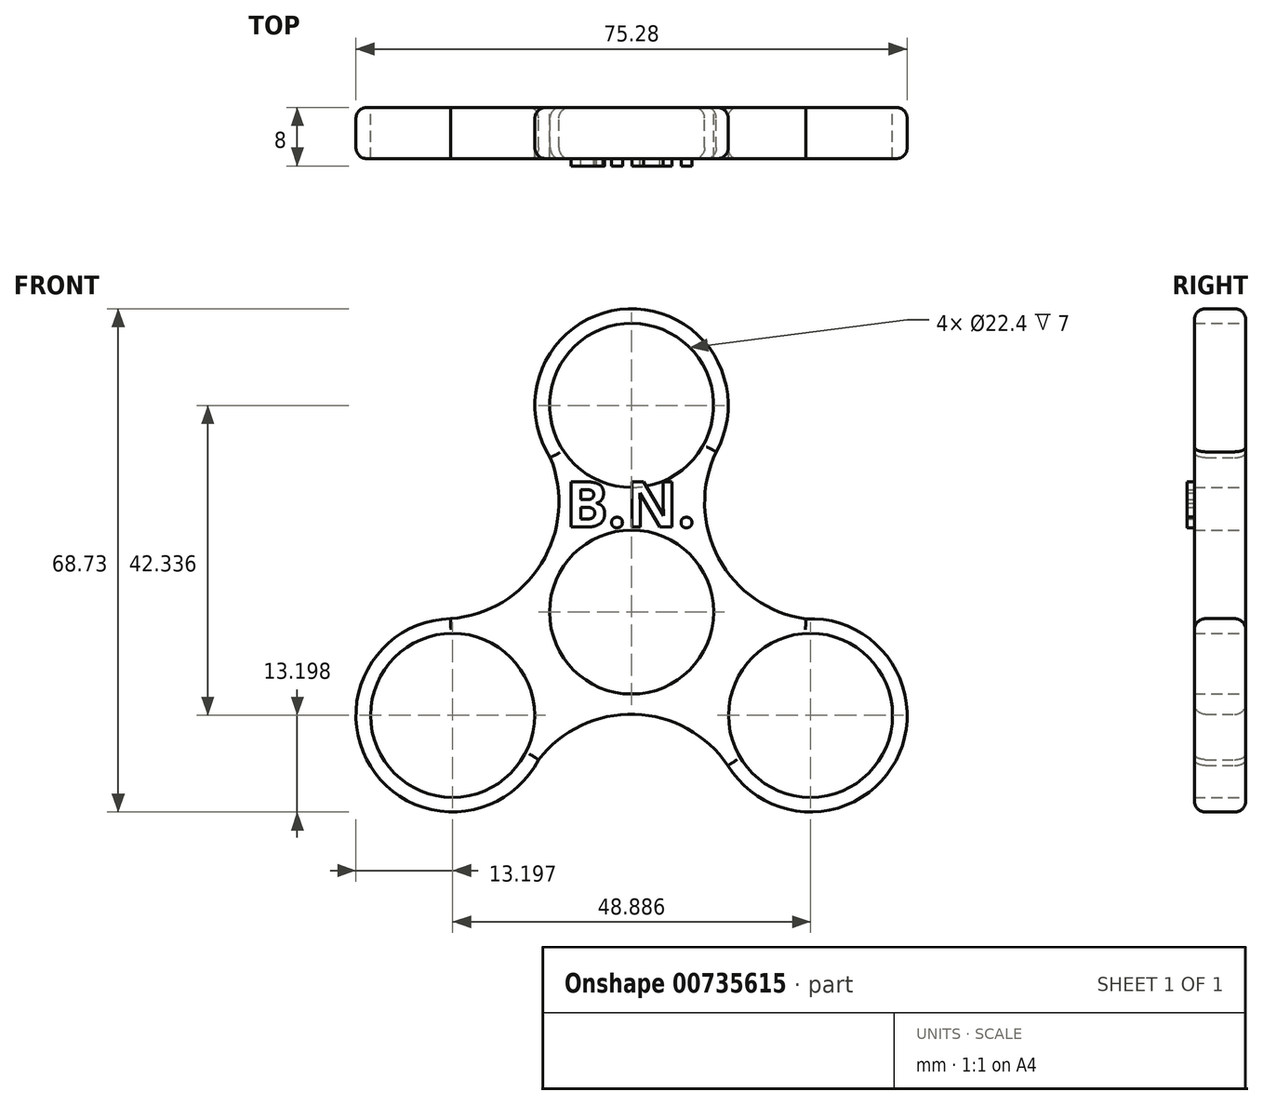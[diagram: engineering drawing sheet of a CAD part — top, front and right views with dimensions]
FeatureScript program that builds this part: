
annotation { "Feature Type Name" : "Feature", "Feature Type Description" : "" }
export const myFeature = defineFeature(function(context is Context, id is Id, definition is map)
    precondition{}
    {
        {
            var Q0;
            Q0=qCreatedBy(makeId("Front.planeOp"),FACE);
            var sketch = newSketch(context, id + "F0", { "sketchPlane" : qUnion([Q0])});
            skCircle(sketch, "E0", {"center": v(0, 0) * mm, "radius": 11.2 * mm});
            skCircle(sketch, "E1", {"center": v(0, 28.22) * mm, "radius": 11.2 * mm});
            skArc(sketch, "E2", {"start": v(11.57, 21.88) * mm, "mid": v(-0.46, 41.42) * mm, "end": v(-11.1, 21.09) * mm});
            skArc(sketch, "E3.1.0", {"start": v(-24.73, -0.92) * mm, "mid": v(-35.64, -21.1) * mm, "end": v(-12.71, -20.16) * mm});
            skCircle(sketch, "E3.1.1", {"center": v(-24.44, -14.11) * mm, "radius": 11.2 * mm});
            skArc(sketch, "E3.2.0", {"start": v(13.16, -20.96) * mm, "mid": v(36.1, -20.3) * mm, "end": v(23.81, -0.93) * mm});
            skCircle(sketch, "E3.2.1", {"center": v(24.44, -14.11) * mm, "radius": 11.2 * mm});
            skLineSegment(sketch, "E4", {"start": v(-12.1, 6.98) * mm, "end": v(-12.22, 7.06) * mm, "construction": true});
            skArc(sketch, "E5", {"start": v(-24.73, -0.92) * mm, "mid": v(-11.3, 8.55) * mm, "end": v(-13.29, 24.86) * mm});
            skArc(sketch, "E6.1.0", {"start": v(13.16, -20.96) * mm, "mid": v(-1.75, -14.06) * mm, "end": v(-14.89, -23.94) * mm});
            skArc(sketch, "E6.2.0", {"start": v(11.57, 21.88) * mm, "mid": v(13.05, 5.5) * mm, "end": v(28.17, -0.92) * mm});
            skLineSegment(sketch, "E7.trimOffspring", {"start": v(-13.27, 5.25) * mm, "end": v(-11.11, 8.98) * mm, "construction": true});
            skLineSegment(sketch, "E8.trimOffspring", {"start": v(-6.6, 16.8) * mm, "end": v(-5.6, 18.52) * mm, "construction": true});
            skSolve(sketch);
        }
        {
            var Q0;
            Q0 = qSketchRegion(id + "F0", true);
            extrude(context, id + "F1", {"entities" : qUnion([Q0]), "depth" : 7 * mm, "offsetDistance" : 25 * mm});
        }
        {
            var Q0;
            Q0=makeQuery(id+"F1.opExtrude","CAP_EDGE",EDGE,{"disambiguationData":[OSD([sQuery(id+"F0.wireOp",EDGE,"E2")])],"isStart":false});
            var Q1;
            Q1=makeQuery(id+"F1.opExtrude","CAP_EDGE",EDGE,{"disambiguationData":[OSD([sQuery(id+"F0.wireOp",EDGE,"E6.2.0")])],"isStart":false});
            var Q2;
            Q2=makeQuery(id+"F1.opExtrude","CAP_EDGE",EDGE,{"disambiguationData":[OSD([sQuery(id+"F0.wireOp",EDGE,"E5")])],"isStart":false});
            var Q3;
            Q3=makeQuery(id+"F1.opExtrude","CAP_EDGE",EDGE,{"disambiguationData":[OSD([sQuery(id+"F0.wireOp",EDGE,"E3.1.0")])],"isStart":false});
            var Q4;
            Q4=makeQuery(id+"F1.opExtrude","CAP_EDGE",EDGE,{"disambiguationData":[OSD([sQuery(id+"F0.wireOp",EDGE,"E6.1.0")])],"isStart":false});
            var Q5;
            Q5=makeQuery(id+"F1.opExtrude","CAP_EDGE",EDGE,{"disambiguationData":[OSD([sQuery(id+"F0.wireOp",EDGE,"E3.2.0")])],"isStart":false});
            fillet(context, id + "F2", {"entities" : qUnion([Q0, Q1, Q2, Q3, Q4, Q5]), "radius" : 1.5 * mm, "tangentPropagation" : true, "allowEdgeOverflow" : false});
        }
        {
            var Q0;
            Q0=makeQuery(id+"F1.opExtrude","CAP_EDGE",EDGE,{"disambiguationData":[OSD([sQuery(id+"F0.wireOp",EDGE,"E2")])],"isStart":true});
            var Q1;
            Q1=makeQuery(id+"F1.opExtrude","CAP_EDGE",EDGE,{"disambiguationData":[OSD([sQuery(id+"F0.wireOp",EDGE,"E6.2.0")])],"isStart":true});
            var Q2;
            Q2=makeQuery(id+"F1.opExtrude","CAP_EDGE",EDGE,{"disambiguationData":[OSD([sQuery(id+"F0.wireOp",EDGE,"E3.2.0")])],"isStart":true});
            var Q3;
            Q3=makeQuery(id+"F1.opExtrude","CAP_EDGE",EDGE,{"disambiguationData":[OSD([sQuery(id+"F0.wireOp",EDGE,"E3.1.0")])],"isStart":true});
            var Q4;
            Q4=makeQuery(id+"F1.opExtrude","CAP_EDGE",EDGE,{"disambiguationData":[OSD([sQuery(id+"F0.wireOp",EDGE,"E6.1.0")])],"isStart":true});
            var Q5;
            Q5=makeQuery(id+"F1.opExtrude","CAP_EDGE",EDGE,{"disambiguationData":[OSD([sQuery(id+"F0.wireOp",EDGE,"E5")])],"isStart":true});
            fillet(context, id + "F3", {"entities" : qUnion([Q0, Q1, Q2, Q3, Q4, Q5]), "radius" : 1.5 * mm, "tangentPropagation" : true, "allowEdgeOverflow" : false});
        }
        {
            var Q0;
            Q0=makeQuery(id+"F1.opExtrude","CAP_FACE",FACE,{"disambiguationData":[OSD([sQuery(id+"F0.wireOp",EDGE,"E0"),sQuery(id+"F0.wireOp",EDGE,"E1"),sQuery(id+"F0.wireOp",EDGE,"E2"),sQuery(id+"F0.wireOp",EDGE,"E3.1.0"),sQuery(id+"F0.wireOp",EDGE,"E3.1.1"),sQuery(id+"F0.wireOp",EDGE,"E3.2.0"),sQuery(id+"F0.wireOp",EDGE,"E3.2.1"),sQuery(id+"F0.wireOp",EDGE,"E5"),sQuery(id+"F0.wireOp",EDGE,"E6.1.0"),sQuery(id+"F0.wireOp",EDGE,"E6.2.0")])],"isStart":false});
            var sketch = newSketch(context, id + "F4", { "sketchPlane" : qUnion([Q0])});
            skText(sketch, "E9", { "text": "B.N.\n", "fontName": "OpenSans-Bold.ttf"});
            const initialGuessF4  = {"E9": [-0.00902, 0.01162, 1, 0, 0.00622]};
            skSetInitialGuess(sketch, initialGuessF4);
            skSolve(sketch);
        }
        {
            var Q0;
            Q0 = qSketchRegion(id + "F4", true);
            extrude(context, id + "F5", {"entities" : qUnion([Q0]), "operationType" : NewBodyOperationType.ADD, "depth" : 1 * mm, "offsetDistance" : 25 * mm});
        }
    });
